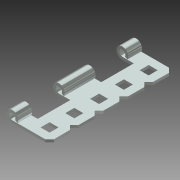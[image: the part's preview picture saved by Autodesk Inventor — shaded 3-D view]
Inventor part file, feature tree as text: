
AUTODESK INVENTOR PART (.ipt)
format: ipt  version: 2013 (Build 170138000, 138)  size: 174,080 bytes
history: native  units: in
note: dims shown in document units (in); Inventor stores cm internally (conversion verified against a paired STEP export)
features: extrude x7, other x5, sketch x3, pattern_linear x1
ambient origin geometry x8: Origin, YZ Plane, XZ Plane, XY Plane, X Axis, Y Axis, Z Axis, Center Point
bodies: Solid1 (feature_tree)
feature tree (16):
  extrude  "Extrusion1"  Depth=0.25in TaperAngle=0.0deg
  extrude  "Extrusion2"  Depth=1.9685in
  pattern_linear  "Rectangular Pattern1"  Spacing1=0.0in  [1 undecoded]
  sketch  "Sketch1"  dims[d0=2.5in d1=0.0in d2=0.25in d3=0.0in]
  sketch  "Sketch2"  dims[d4=0.25in d5=0.0in d6=1.9685in d8=0.5in]
  sketch  "Sketch3"  dims[d9=0.0in d10=0.0in d11=0.0in d12=0.0in d13=0.0in d14=0.0in d15=0.0in d16=0.0in d17=0.0in d18=0.0in]
  other  "Srf1"
  other  "Srf2"
  other  "Srf3"
  other  "Srf4"
  other  "Srf5"
  extrude  "ExtrusionSrf1"  TaperAngle=0.0deg  [1 undecoded]
  extrude  "ExtrusionSrf2"  TaperAngle=0.0deg  [1 undecoded]
  extrude  "ExtrusionSrf3"  TaperAngle=0.0deg  [1 undecoded]
  extrude  "ExtrusionSrf4"  TaperAngle=0.0deg  [1 undecoded]
  extrude  "ExtrusionSrf5"  TaperAngle=0.0deg  [1 undecoded]
note: 6 required parameter values undecoded (feature->parameter linkage not recoverable at this tier; creation-order binding heuristic only, values carry confidence <= 0.55)
